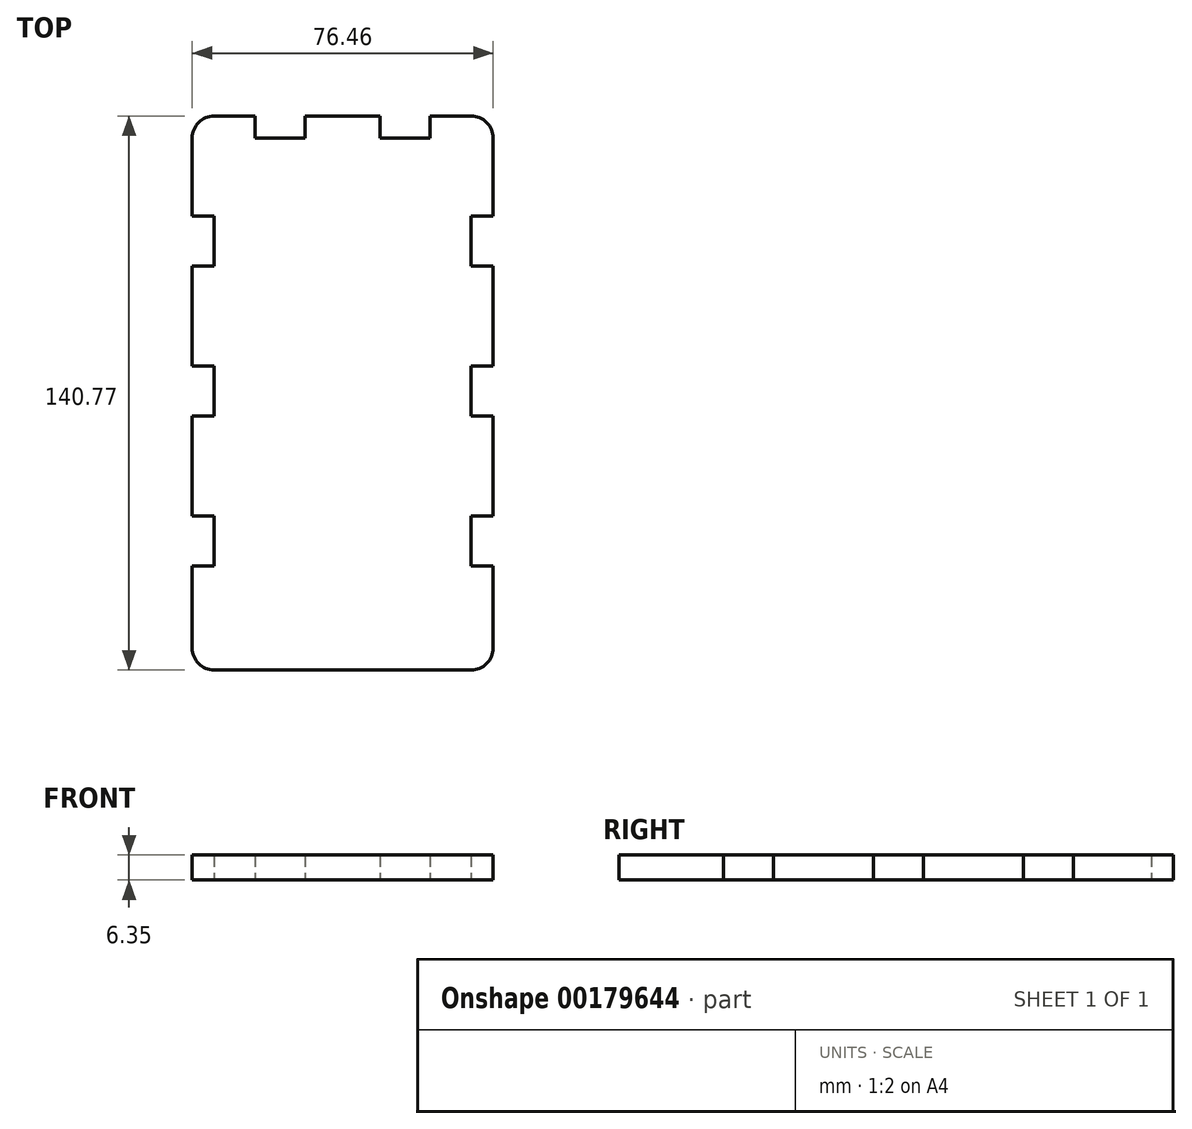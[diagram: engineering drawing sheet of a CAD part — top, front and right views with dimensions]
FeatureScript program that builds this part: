
annotation { "Feature Type Name" : "Feature", "Feature Type Description" : "" }
export const myFeature = defineFeature(function(context is Context, id is Id, definition is map)
    precondition{}
    {
        {
            var Q0;
            Q0=qCreatedBy(makeId("Top.planeOp"),FACE);
            var sketch = newSketch(context, id + "F0", { "sketchPlane" : qUnion([Q0])});
            skLineSegment(sketch, "E0.0", {"start": v(-32.64, 68.88) * mm, "end": v(-22.23, 68.88) * mm});
            skLineSegment(sketch, "E0.1", {"start": v(-38.23, 63.29) * mm, "end": v(-38.23, 43.48) * mm});
            skLineSegment(sketch, "E0.2", {"start": v(-32.64, -71.9) * mm, "end": v(-22.23, -71.9) * mm});
            skLineSegment(sketch, "E0.3", {"start": v(38.23, 63.29) * mm, "end": v(38.23, 43.48) * mm});
            skPoint(sketch, "E1", {"position": v(-38.23, 43.48) * mm});
            skPoint(sketch, "E2", {"position": v(38.23, 43.48) * mm});
            skPoint(sketch, "E3", {"position": v(-38.23, 30.78) * mm});
            skPoint(sketch, "E4", {"position": v(38.23, 30.78) * mm});
            skLineSegment(sketch, "E5", {"start": v(-38.23, 43.48) * mm, "end": v(-32.64, 43.48) * mm});
            skLineSegment(sketch, "E6", {"start": v(-38.23, 30.78) * mm, "end": v(-32.64, 30.78) * mm});
            skLineSegment(sketch, "E7", {"start": v(-32.64, 30.78) * mm, "end": v(-32.64, 43.48) * mm});
            skLineSegment(sketch, "E8.trimOffspring", {"start": v(-38.23, 30.78) * mm, "end": v(-38.23, 5.38) * mm});
            skLineSegment(sketch, "E9", {"start": v(38.23, 43.48) * mm, "end": v(32.64, 43.48) * mm});
            skLineSegment(sketch, "E10", {"start": v(38.23, 30.78) * mm, "end": v(32.64, 30.78) * mm});
            skLineSegment(sketch, "E11", {"start": v(32.64, 30.78) * mm, "end": v(32.64, 43.48) * mm});
            skLineSegment(sketch, "E12.trimOffspring", {"start": v(38.23, 30.78) * mm, "end": v(38.23, 5.38) * mm});
            skPoint(sketch, "E13", {"position": v(-38.23, 5.38) * mm});
            skPoint(sketch, "E14", {"position": v(38.23, 5.38) * mm});
            skPoint(sketch, "E15", {"position": v(-38.23, -7.32) * mm});
            skPoint(sketch, "E16", {"position": v(38.23, -7.32) * mm});
            skPoint(sketch, "E17", {"position": v(-38.23, -32.72) * mm});
            skPoint(sketch, "E18", {"position": v(38.23, -32.72) * mm});
            skPoint(sketch, "E19", {"position": v(38.23, -45.42) * mm});
            skLineSegment(sketch, "E20", {"start": v(-38.23, 5.38) * mm, "end": v(-32.64, 5.38) * mm});
            skLineSegment(sketch, "E21", {"start": v(-38.23, -7.32) * mm, "end": v(-32.64, -7.32) * mm});
            skLineSegment(sketch, "E22", {"start": v(-32.64, -7.32) * mm, "end": v(-32.64, 5.38) * mm});
            skLineSegment(sketch, "E23.trimOffspring", {"start": v(-38.23, -7.32) * mm, "end": v(-38.23, -32.72) * mm});
            skLineSegment(sketch, "E24.trimOffspring", {"start": v(-38.23, -52.57) * mm, "end": v(-38.23, -66.3) * mm});
            skLineSegment(sketch, "E25", {"start": v(-38.23, -32.72) * mm, "end": v(-32.64, -32.72) * mm});
            skLineSegment(sketch, "E26", {"start": v(-38.23, -45.42) * mm, "end": v(-32.64, -45.42) * mm});
            skLineSegment(sketch, "E27", {"start": v(-32.64, -45.42) * mm, "end": v(-32.64, -32.72) * mm});
            skLineSegment(sketch, "E28", {"start": v(38.23, 5.38) * mm, "end": v(32.64, 5.38) * mm});
            skLineSegment(sketch, "E29", {"start": v(38.23, -7.32) * mm, "end": v(32.64, -7.32) * mm});
            skLineSegment(sketch, "E30", {"start": v(32.64, -7.32) * mm, "end": v(32.64, 5.38) * mm});
            skLineSegment(sketch, "E31.trimOffspring", {"start": v(38.23, -7.32) * mm, "end": v(38.23, -32.72) * mm});
            skLineSegment(sketch, "E32", {"start": v(38.23, -32.72) * mm, "end": v(32.64, -32.72) * mm});
            skLineSegment(sketch, "E33", {"start": v(38.23, -45.42) * mm, "end": v(32.64, -45.42) * mm});
            skLineSegment(sketch, "E34", {"start": v(32.64, -45.42) * mm, "end": v(32.64, -32.72) * mm});
            skLineSegment(sketch, "E35.trimOffspring", {"start": v(38.23, -52.57) * mm, "end": v(38.23, -66.3) * mm});
            skLineSegment(sketch, "E36", {"start": v(-38.23, -45.42) * mm, "end": v(-38.23, -52.57) * mm});
            skLineSegment(sketch, "E37", {"start": v(38.23, -45.42) * mm, "end": v(38.23, -52.57) * mm});
            skPoint(sketch, "E38", {"position": v(-22.23, 68.88) * mm});
            skPoint(sketch, "E39", {"position": v(-9.53, 68.88) * mm});
            skPoint(sketch, "E40", {"position": v(9.52, 68.88) * mm});
            skPoint(sketch, "E41", {"position": v(22.22, 68.88) * mm});
            skLineSegment(sketch, "E42", {"start": v(-22.23, 68.88) * mm, "end": v(-22.23, 63.29) * mm});
            skLineSegment(sketch, "E43", {"start": v(-9.53, 68.88) * mm, "end": v(-9.53, 63.29) * mm});
            skLineSegment(sketch, "E44", {"start": v(-9.53, 63.29) * mm, "end": v(-22.23, 63.29) * mm});
            skLineSegment(sketch, "E45.trimOffspring", {"start": v(-9.53, 68.88) * mm, "end": v(9.52, 68.88) * mm});
            skLineSegment(sketch, "E46", {"start": v(9.52, 68.88) * mm, "end": v(9.52, 63.29) * mm});
            skLineSegment(sketch, "E47", {"start": v(22.22, 68.88) * mm, "end": v(22.22, 63.29) * mm});
            skLineSegment(sketch, "E48.trimOffspring", {"start": v(22.22, 68.88) * mm, "end": v(32.64, 68.88) * mm});
            skLineSegment(sketch, "E49", {"start": v(9.52, 63.29) * mm, "end": v(22.22, 63.29) * mm});
            skLineSegment(sketch, "E50.trimOffspring", {"start": v(-9.53, -71.9) * mm, "end": v(10.29, -71.9) * mm});
            skLineSegment(sketch, "E51.trimOffspring", {"start": v(22.99, -71.9) * mm, "end": v(32.64, -71.9) * mm});
            skPoint(sketch, "E52.visualSharp", {"position": v(-38.23, 68.88) * mm});
            skArc(sketch, "E52.filletArc", {"start": v(-32.64, 68.88) * mm, "mid": v(-36.6, 67.24) * mm, "end": v(-38.23, 63.29) * mm});
            skPoint(sketch, "E53.visualSharp", {"position": v(38.23, 68.88) * mm});
            skArc(sketch, "E53.filletArc", {"start": v(38.23, 63.29) * mm, "mid": v(36.6, 67.24) * mm, "end": v(32.64, 68.88) * mm});
            skPoint(sketch, "E54.visualSharp", {"position": v(38.23, -71.9) * mm});
            skArc(sketch, "E54.filletArc", {"start": v(32.64, -71.9) * mm, "mid": v(36.6, -70.25) * mm, "end": v(38.23, -66.3) * mm});
            skPoint(sketch, "E55.visualSharp", {"position": v(-38.23, -71.9) * mm});
            skArc(sketch, "E55.filletArc", {"start": v(-38.23, -66.3) * mm, "mid": v(-36.6, -70.25) * mm, "end": v(-32.64, -71.9) * mm});
            skLineSegment(sketch, "E56", {"start": v(-32.64, -71.9) * mm, "end": v(32.64, -71.9) * mm});
            skSolve(sketch);
        }
        {
            var Q0;
            Q0=makeQuery(id+"F0.imprint","IMPRINT",FACE,{"disambiguationData":[TD([[makeQuery(id+"F0.imprint","IMPRINT",EDGE,{"derivedFrom":sQuery(id+"F0.wireOp",EDGE,"E0.0")}),-1.0]])]});
            extrude(context, id + "F1", {"entities" : qUnion([Q0]), "depth" : 6.35 * mm});
        }
    });
